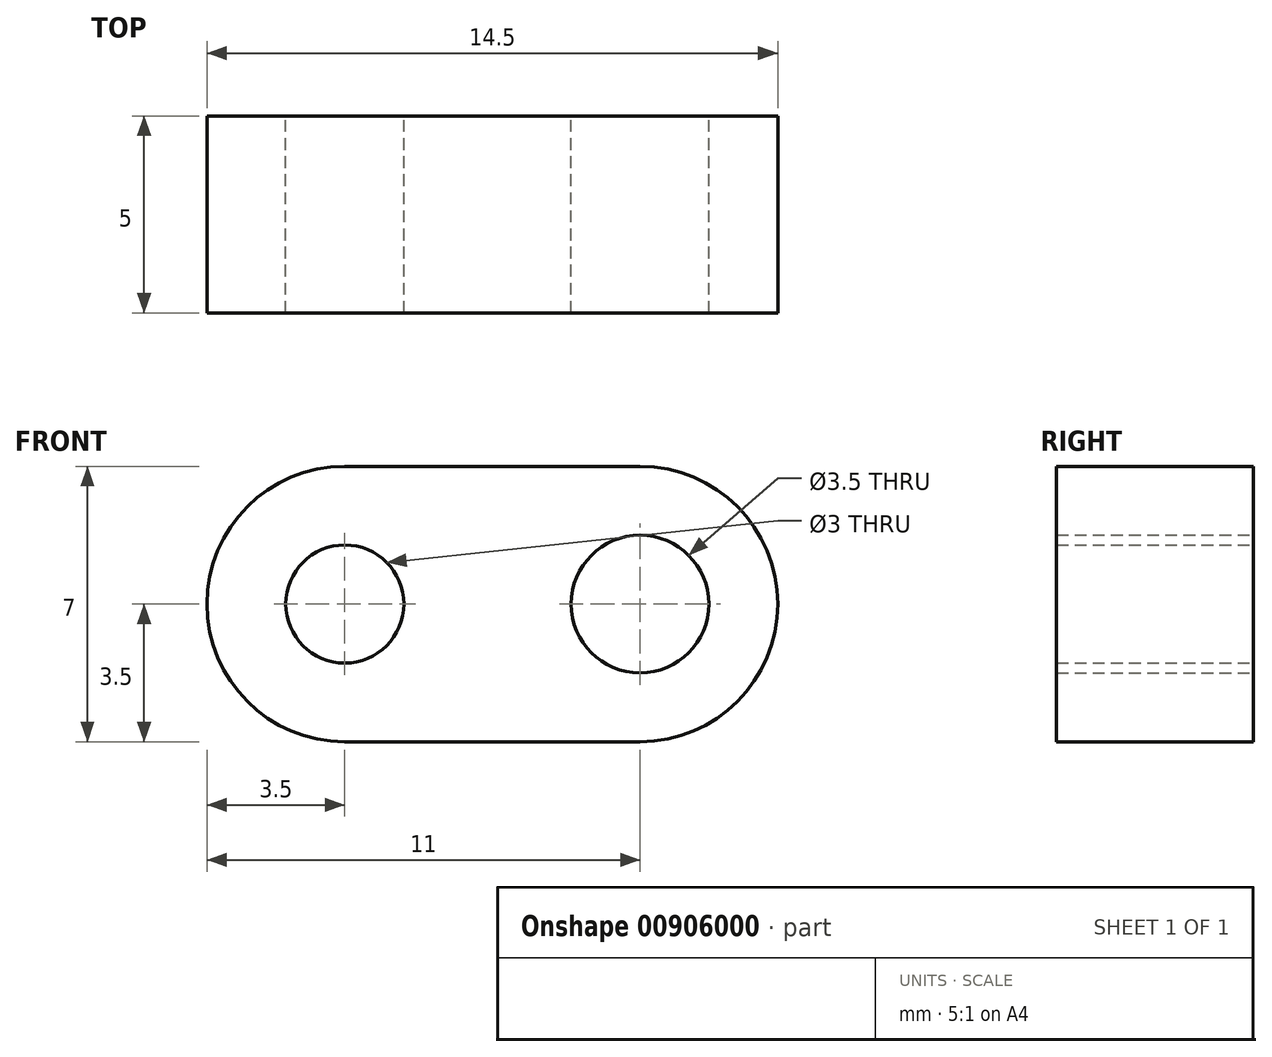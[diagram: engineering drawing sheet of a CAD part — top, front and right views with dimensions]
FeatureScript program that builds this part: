
annotation { "Feature Type Name" : "Feature", "Feature Type Description" : "" }
export const myFeature = defineFeature(function(context is Context, id is Id, definition is map)
    precondition{}
    {
        {
            var Q0;
            Q0=qCreatedBy(makeId("Front.planeOp"),FACE);
            var sketch = newSketch(context, id + "F0", { "sketchPlane" : qUnion([Q0])});
            skArc(sketch, "E0", {"start": v(-3.75, 3.5) * mm, "mid": v(-7.25, 0) * mm, "end": v(-3.75, -3.5) * mm});
            skArc(sketch, "E1", {"start": v(3.75, -3.5) * mm, "mid": v(7.25, 0) * mm, "end": v(3.75, 3.5) * mm});
            skLineSegment(sketch, "E2", {"start": v(-3.75, 3.5) * mm, "end": v(3.75, 3.5) * mm});
            skLineSegment(sketch, "E3", {"start": v(3.75, -3.5) * mm, "end": v(-3.75, -3.5) * mm});
            skCircle(sketch, "E4", {"center": v(3.75, 0) * mm, "radius": 1.75 * mm});
            skCircle(sketch, "E5", {"center": v(-3.75, 0) * mm, "radius": 1.5 * mm});
            skSolve(sketch);
        }
        {
            var Q0;
            Q0=qSketchRegion(id+"F0",true);
            extrude(context, id + "F1", {"entities" : qUnion([Q0]), "endBound" : BoundingType.SYMMETRIC, "depth" : 5 * mm, "offsetDistance" : 25.4 * mm});
        }
    });
